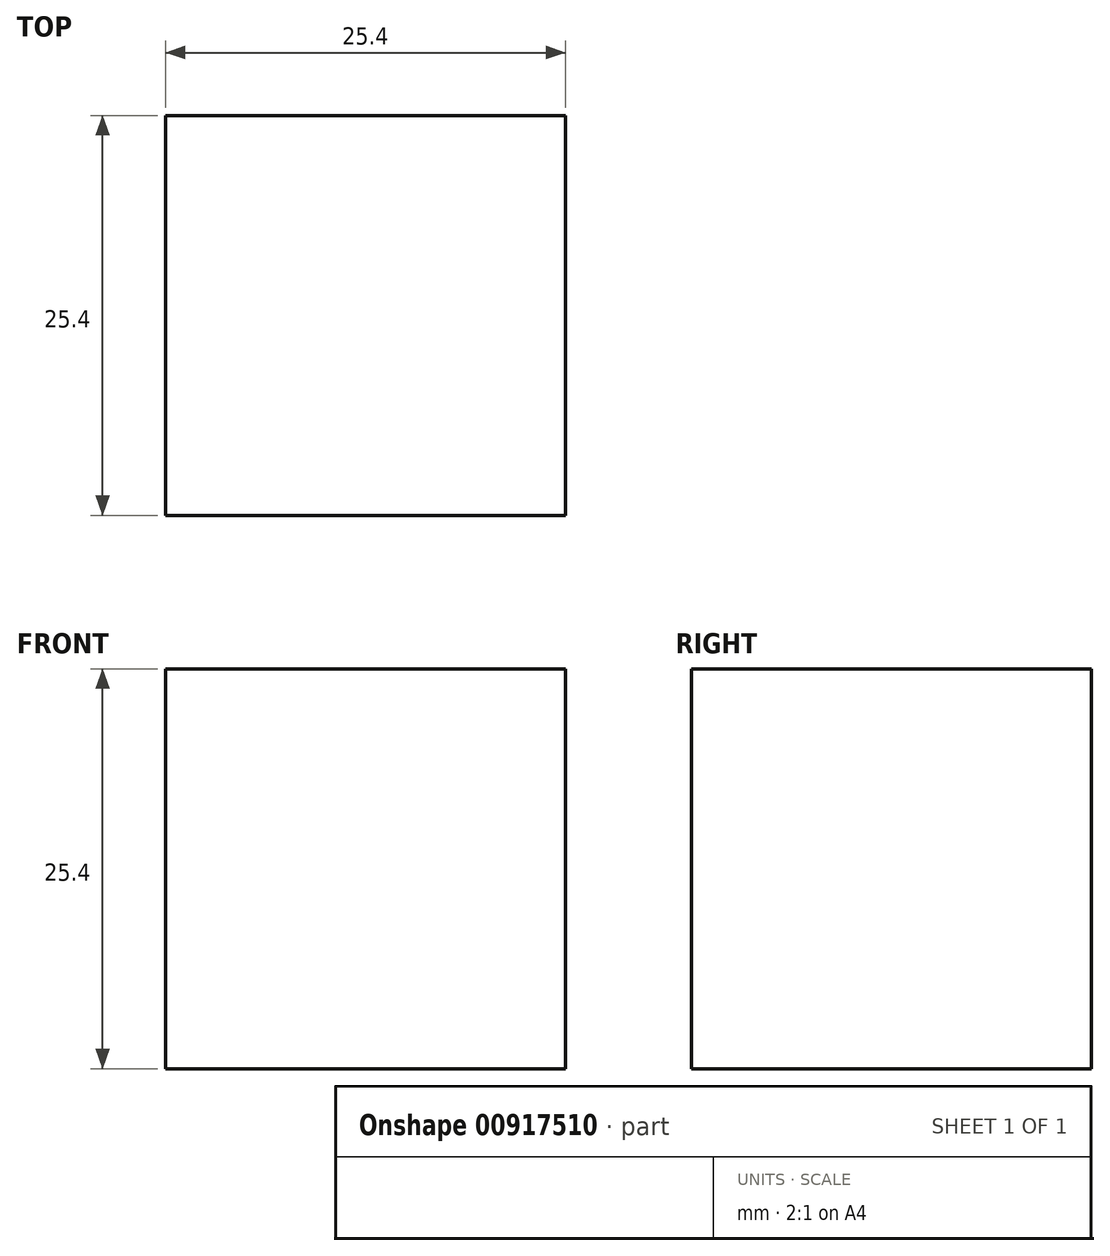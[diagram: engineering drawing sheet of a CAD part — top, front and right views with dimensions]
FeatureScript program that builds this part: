
annotation { "Feature Type Name" : "Feature", "Feature Type Description" : "" }
export const myFeature = defineFeature(function(context is Context, id is Id, definition is map)
    precondition{}
    {
        {
            var Q0;
            Q0=qCreatedBy(makeId("Top.planeOp"),FACE);
            var sketch = newSketch(context, id + "F0", { "sketchPlane" : qUnion([Q0])});
            skLineSegment(sketch, "E0.bottom", {"start": v(-12.7, 12.7) * mm, "end": v(12.7, 12.7) * mm});
            skLineSegment(sketch, "E0.top", {"start": v(-12.7, -12.7) * mm, "end": v(12.7, -12.7) * mm});
            skLineSegment(sketch, "E0.left", {"start": v(-12.7, 12.7) * mm, "end": v(-12.7, -12.7) * mm});
            skLineSegment(sketch, "E0.right", {"start": v(12.7, 12.7) * mm, "end": v(12.7, -12.7) * mm});
            skPoint(sketch, "E0.middle", {"position": v(0, 0) * mm});
            skSolve(sketch);
        }
        {
            var Q0;
            Q0 = qSketchRegion(id + "F0", true);
            extrude(context, id + "F1", {"entities" : qUnion([Q0]), "depth" : 25.4 * mm, "offsetDistance" : 25 * mm});
        }
    });
